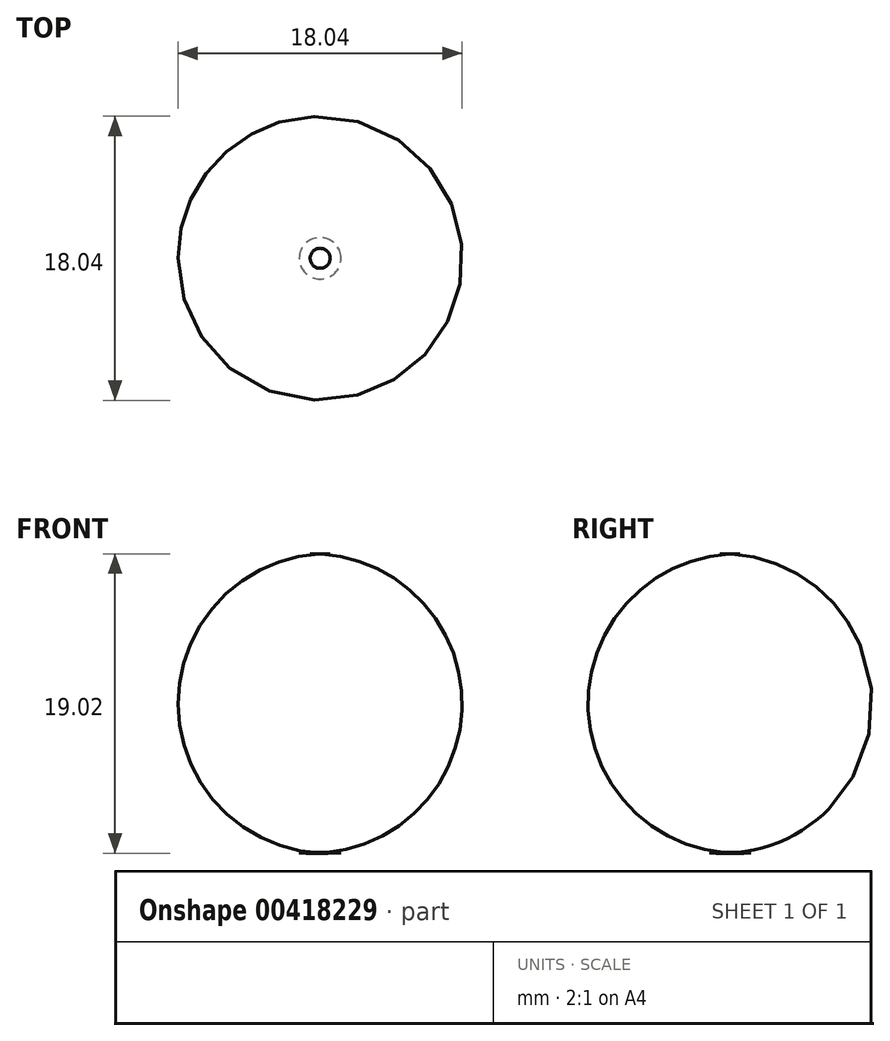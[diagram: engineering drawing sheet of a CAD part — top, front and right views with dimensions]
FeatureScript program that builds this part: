
annotation { "Feature Type Name" : "Feature", "Feature Type Description" : "" }
export const myFeature = defineFeature(function(context is Context, id is Id, definition is map)
    precondition{}
    {
        {
            var Q0;
            Q0=qCreatedBy(makeId("Front.planeOp"),FACE);
            var sketch = newSketch(context, id + "F0", { "sketchPlane" : qUnion([Q0])});
            skLineSegment(sketch, "E0", {"start": v(0, 11.8) * mm, "end": v(0, -13.81) * mm});
            skArc(sketch, "E1", {"start": v(0, -13.81) * mm, "mid": v(13.74, -1) * mm, "end": v(0, 11.8) * mm});
            skSolve(sketch);
        }
        {
            var Q0;
            Q0=makeQuery(id+"F0.imprint","IMPRINT",FACE,{"disambiguationData":[TD([[makeQuery(id+"F0.imprint","IMPRINT",EDGE,{"derivedFrom":sQuery(id+"F0.wireOp",EDGE,"E0")}),1.0]])]});
            var Q1;
            Q1=sQuery(id+"F0.wireOp",EDGE,"E0");
            revolve(context, id + "F1", {"entities" : qUnion([Q0]), "axis" : qUnion([Q1]), "revolveType" : RevolveType.FULL});
        }
        {
            var Q0;
            Q0=qCreatedBy(makeId("Front.planeOp"),FACE);
            var sketch = newSketch(context, id + "F2", { "sketchPlane" : qUnion([Q0])});
            skLineSegment(sketch, "E2", {"start": v(0, 11.8) * mm, "end": v(0, 30.8) * mm});
            skArc(sketch, "E3", {"start": v(0, 11.8) * mm, "mid": v(10, 21.3) * mm, "end": v(0, 30.8) * mm});
            skSolve(sketch);
        }
        {
            var Q0;
            Q0=makeQuery(id+"F2.imprint","IMPRINT",FACE,{"disambiguationData":[TD([[makeQuery(id+"F2.imprint","IMPRINT",EDGE,{"derivedFrom":sQuery(id+"F2.wireOp",EDGE,"E2")}),-1.0]])]});
            var Q1;
            Q1=sQuery(id+"F2.wireOp",EDGE,"E2");
            revolve(context, id + "F3", {"operationType" : NewBodyOperationType.ADD, "entities" : qUnion([Q0]), "axis" : qUnion([Q1]), "revolveType" : RevolveType.FULL});
        }
        {
            var Q0;
            Q0=qCreatedBy(makeId("Front.planeOp"),FACE);
            var sketch = newSketch(context, id + "F4", { "sketchPlane" : qUnion([Q0])});
            skLineSegment(sketch, "E4", {"start": v(0, 30.8) * mm, "end": v(0, 43.75) * mm});
            skArc(sketch, "E5", {"start": v(0, 30.8) * mm, "mid": v(6.68, 37.27) * mm, "end": v(0, 43.75) * mm});
            skSolve(sketch);
        }
        {
            var Q0;
            Q0=makeQuery(id+"F4.imprint","IMPRINT",FACE,{"disambiguationData":[TD([[makeQuery(id+"F4.imprint","IMPRINT",EDGE,{"derivedFrom":sQuery(id+"F4.wireOp",EDGE,"E4")}),-1.0]])]});
            var Q1;
            Q1=sQuery(id+"F4.wireOp",EDGE,"E4");
            revolve(context, id + "F5", {"operationType" : NewBodyOperationType.ADD, "entities" : qUnion([Q0]), "axis" : qUnion([Q1]), "revolveType" : RevolveType.FULL});
        }
    });
